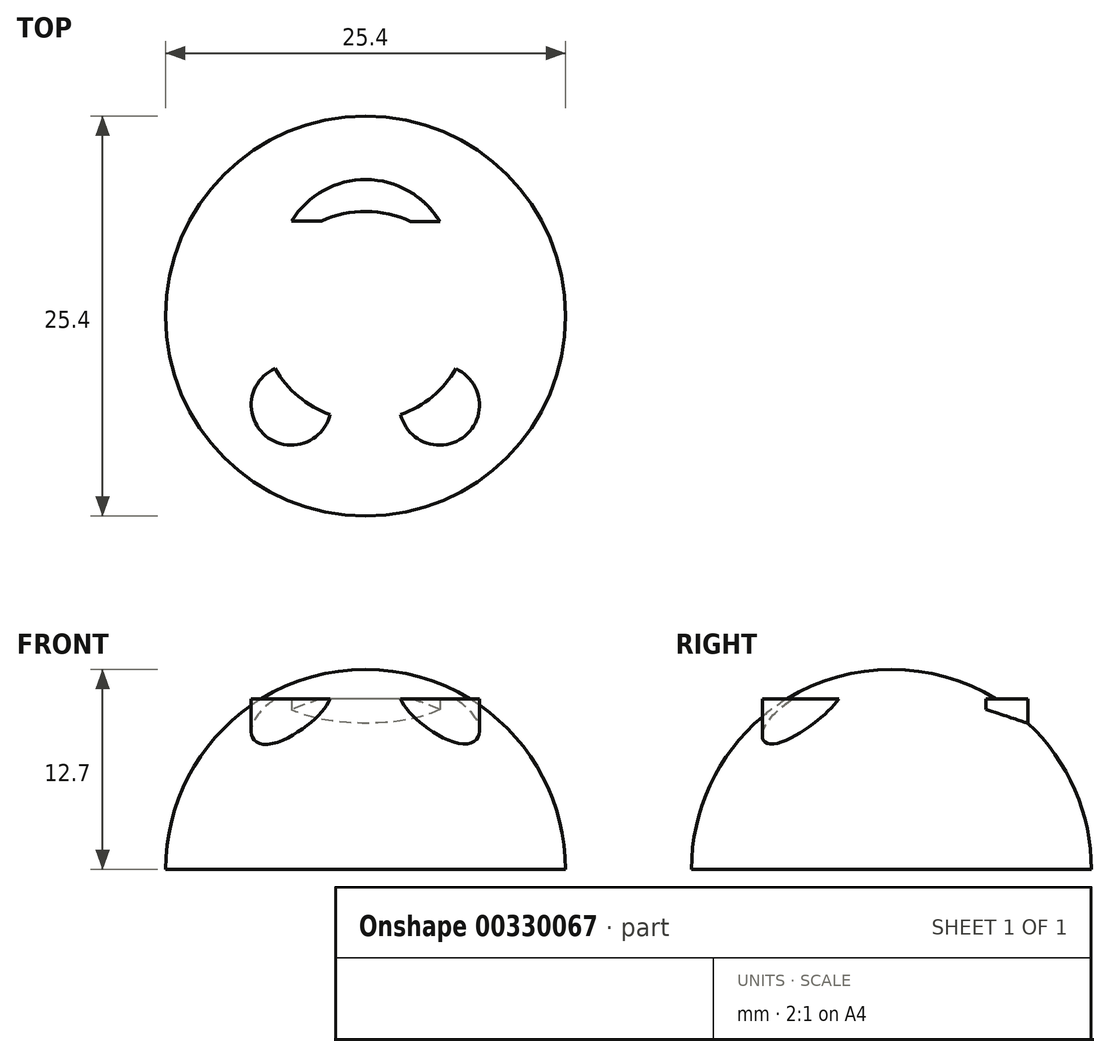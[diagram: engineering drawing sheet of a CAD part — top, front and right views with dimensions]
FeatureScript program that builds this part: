
annotation { "Feature Type Name" : "Feature", "Feature Type Description" : "" }
export const myFeature = defineFeature(function(context is Context, id is Id, definition is map)
    precondition{}
    {
        {
            var Q0;
            Q0=qCreatedBy(makeId("Top.planeOp"),FACE);
            var sketch = newSketch(context, id + "F0", { "sketchPlane" : qUnion([Q0])});
            skCircle(sketch, "E0", {"center": v(0, 0) * mm, "radius": 12.7 * mm});
            skLineSegment(sketch, "E1", {"start": v(0, 0) * mm, "end": v(0, -12.7) * mm});
            skLineSegment(sketch, "E2", {"start": v(0, -12.7) * mm, "end": v(0, 12.7) * mm});
            skSolve(sketch);
        }
        {
            var Q0;
            {var subQ0=sQuery(id+"F0.wireOp",EDGE,"E2");var subQ4=makeQuery(id+"F0.imprint","IMPRINT",VERTEX,{"derivedFrom":subQ0});Q0=makeQuery(id+"F0.imprint","IMPRINT",FACE,{"disambiguationData":[TD([[makeQuery(id+"F0.imprint","IMPRINT",EDGE,{"disambiguationData":[TD([[subQ4,1.0]])],"derivedFrom":subQ0}),1.0]])]});}
            var Q1;
            Q1=sQuery(id+"F0.wireOp",EDGE,"E2");
            revolve(context, id + "F1", {"entities" : qUnion([Q0]), "axis" : qUnion([Q1]), "revolveType" : RevolveType.ONE_DIRECTION, "angle" : 180 * degree});
        }
        {
            var Q0;
            Q0=qCreatedBy(makeId("Top.planeOp"),FACE);
            var sketch = newSketch(context, id + "F2", { "sketchPlane" : qUnion([Q0])});
            skCircle(sketch, "E3", {"center": v(-4.72, -5.66) * mm, "radius": 2.54 * mm});
            skCircle(sketch, "E4", {"center": v(4.7, -5.66) * mm, "radius": 2.54 * mm});
            skSolve(sketch);
        }
        {
            var Q0;
            Q0=qCreatedBy(makeId("Top.planeOp"),FACE);
            var sketch = newSketch(context, id + "F3", { "sketchPlane" : qUnion([Q0])});
            skLineSegment(sketch, "E5", {"start": v(-4.68, -5.58) * mm, "end": v(-4.68, 6.05) * mm});
            skLineSegment(sketch, "E6", {"start": v(4.72, -5.58) * mm, "end": v(4.72, 6) * mm});
            skLineSegment(sketch, "E7", {"start": v(4.72, 6) * mm, "end": v(-4.68, 6.05) * mm});
            skArc(sketch, "E8", {"start": v(4.72, 6) * mm, "mid": v(0.03, 8.67) * mm, "end": v(-4.68, 6.05) * mm});
            skSolve(sketch);
        }
        {
            var Q0;
            Q0=makeQuery(id+"F3.imprint","IMPRINT",FACE,{"disambiguationData":[TD([[makeQuery(id+"F3.imprint","IMPRINT",EDGE,{"derivedFrom":sQuery(id+"F3.wireOp",EDGE,"E7")}),-1.0]])]});
            var Q1;
            Q1=makeQuery(id+"F2.imprint","IMPRINT",FACE,{"disambiguationData":[TD([[makeQuery(id+"F2.imprint","IMPRINT",EDGE,{"derivedFrom":sQuery(id+"F2.wireOp",EDGE,"E4")}),1.0]])]});
            var Q2;
            Q2=makeQuery(id+"F2.imprint","IMPRINT",FACE,{"disambiguationData":[TD([[makeQuery(id+"F2.imprint","IMPRINT",EDGE,{"derivedFrom":sQuery(id+"F2.wireOp",EDGE,"E3")}),1.0]])]});
            extrude(context, id + "F4", {"entities" : qUnion([Q0, Q1, Q2]), "operationType" : NewBodyOperationType.ADD, "depth" : 10.82 * mm});
        }
    });
